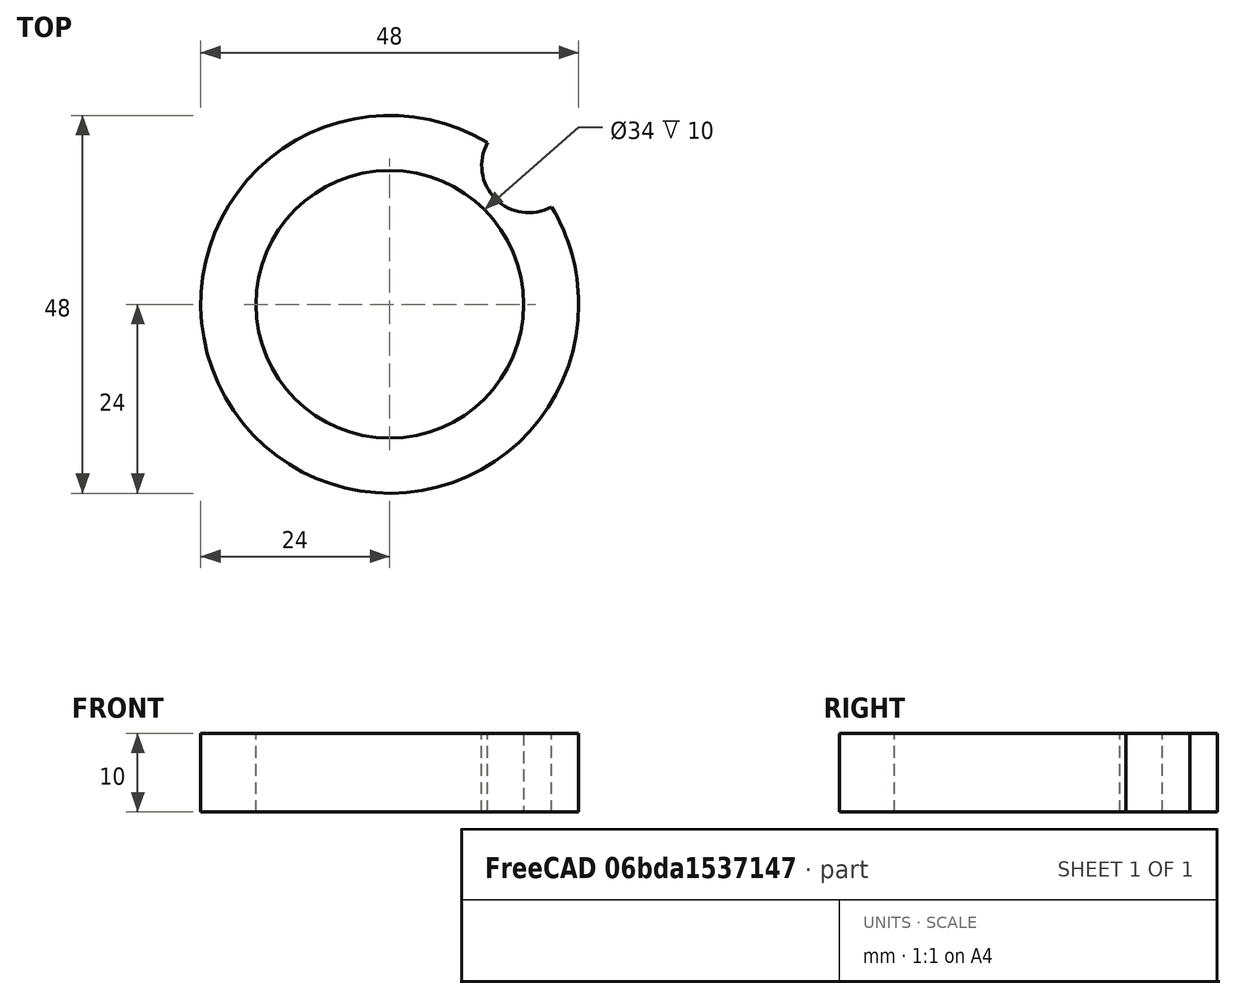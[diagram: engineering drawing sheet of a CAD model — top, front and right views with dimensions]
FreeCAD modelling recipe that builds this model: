
FCSTD DOCUMENT  (FreeCAD 0.17R13541 (Git))
Label: slice_airation_chamber_inner_ring
License: All rights reserved
LicenseURL: http://en.wikipedia.org/wiki/All_rights_reserved
objects: Sketcher::SketchObject×2, PartDesign::Pad×1, PartDesign::Pocket×1, PartDesign::Body×1
note: 7 computed .brp shape members not serialized (recipe doc carries the construction recipe); baked Part::Feature solids carry a one-line shape summary decoded from their .brp

FEATURE [Sketcher::SketchObject] Sketch003
  MapMode = 5
  Support = -> [XY_Plane]
  sketch-geometry (2):
    g0: Circle CenterX=0 CenterY=0 CenterZ=0 NormalX=0 NormalY=0 NormalZ=1 AngleXU=0 Radius=24
    g1: Circle CenterX=0 CenterY=0 CenterZ=0 NormalX=0 NormalY=0 NormalZ=1 AngleXU=0 Radius=17
  constraints (3):
    c: Coincident(g0,g-1)
    c: Radius(g0) = 24
    c: Radius(g1) = 17
FEATURE [PartDesign::Pad] Pad
  Length = 10
  Length2 = 100
  Profile = -> Sketch003
  Reversed = true
  Type = 0
FEATURE [Sketcher::SketchObject] Sketch005
  MapMode = 5
  Support = -> [XY_Plane]
  sketch-geometry (1):
    g0: Circle CenterX=17.6814 CenterY=17.6324 CenterZ=0 NormalX=0 NormalY=0 NormalZ=1 AngleXU=0 Radius=6
  constraints (1):
    c: Radius(g0) = 6
FEATURE [PartDesign::Pocket] Pocket
  BaseFeature = -> Pad
  Length = 5
  Length2 = 100
  Midplane = true
  Profile = -> Sketch005
  Type = 1
FEATURE [PartDesign::Body] Body
  Group = -> [Sketch003,Pad,Sketch005,Pocket]
  Origin = -> Origin
  Tip = -> Pocket
